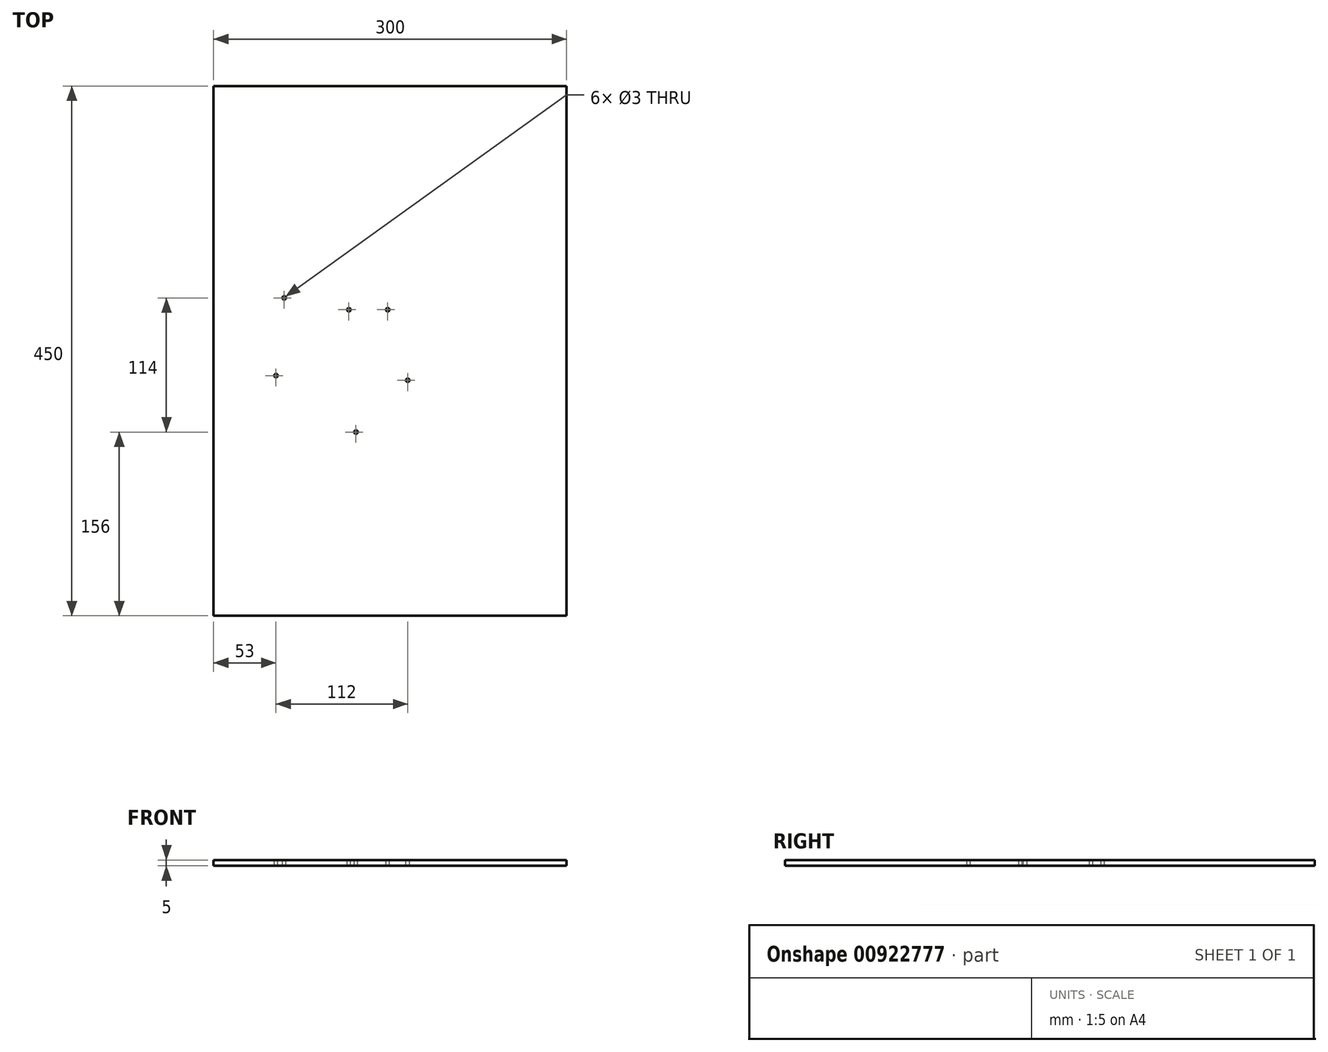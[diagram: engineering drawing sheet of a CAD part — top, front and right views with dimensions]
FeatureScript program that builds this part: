
annotation { "Feature Type Name" : "Feature", "Feature Type Description" : "" }
export const myFeature = defineFeature(function(context is Context, id is Id, definition is map)
    precondition{}
    {
        {
            var Q0;
            Q0=qCreatedBy(makeId("Top.planeOp"),FACE);
            var sketch = newSketch(context, id + "F0", { "sketchPlane" : qUnion([Q0])});
            skLineSegment(sketch, "E0.bottom", {"start": v(-150, 225) * mm, "end": v(150, 225) * mm});
            skLineSegment(sketch, "E0.top", {"start": v(-150, -225) * mm, "end": v(150, -225) * mm});
            skLineSegment(sketch, "E0.left", {"start": v(-150, 225) * mm, "end": v(-150, -225) * mm});
            skLineSegment(sketch, "E0.right", {"start": v(150, 225) * mm, "end": v(150, -225) * mm});
            skSolve(sketch);
        }
        {
            var Q0;
            Q0=makeQuery(id+"F0.imprint","IMPRINT",FACE,{"disambiguationData":[TD([[makeQuery(id+"F0.imprint","IMPRINT",EDGE,{"derivedFrom":sQuery(id+"F0.wireOp",EDGE,"E0.bottom")}),-1.0]])]});
            extrude(context, id + "F1", {"entities" : qUnion([Q0]), "depth" : 5 * mm, "offsetDistance" : 25.4 * mm});
        }
        {
            var Q0;
            Q0=makeQuery(id+"F1.opExtrude","CAP_FACE",FACE,{"disambiguationData":[OSD([sQuery(id+"F0.wireOp",EDGE,"E0.bottom"),sQuery(id+"F0.wireOp",EDGE,"E0.top"),sQuery(id+"F0.wireOp",EDGE,"E0.left"),sQuery(id+"F0.wireOp",EDGE,"E0.right")])],"isStart":false});
            var sketch = newSketch(context, id + "F2", { "sketchPlane" : qUnion([Q0])});
            skCircle(sketch, "E1", {"center": v(-90, 45) * mm, "radius": 1.5 * mm});
            skCircle(sketch, "E2", {"center": v(-97, -21) * mm, "radius": 1.5 * mm});
            skCircle(sketch, "E3", {"center": v(-35, 35) * mm, "radius": 1.5 * mm});
            skCircle(sketch, "E4", {"center": v(-2, 35) * mm, "radius": 1.5 * mm});
            skCircle(sketch, "E5", {"center": v(-29, -69) * mm, "radius": 1.5 * mm});
            skCircle(sketch, "E6", {"center": v(15, -25) * mm, "radius": 1.5 * mm});
            skLineSegment(sketch, "E7", {"start": v(-199.4, 75) * mm, "end": v(183.12, 75) * mm});
            skSolve(sketch);
        }
        {
            var Q0;
            Q0 = qSketchRegion(id + "F2", true);
            extrude(context, id + "F3", {"entities" : qUnion([Q0]), "operationType" : NewBodyOperationType.REMOVE, "oppositeDirection" : true, "depth" : 25 * mm, "offsetDistance" : 25 * mm});
        }
    });
